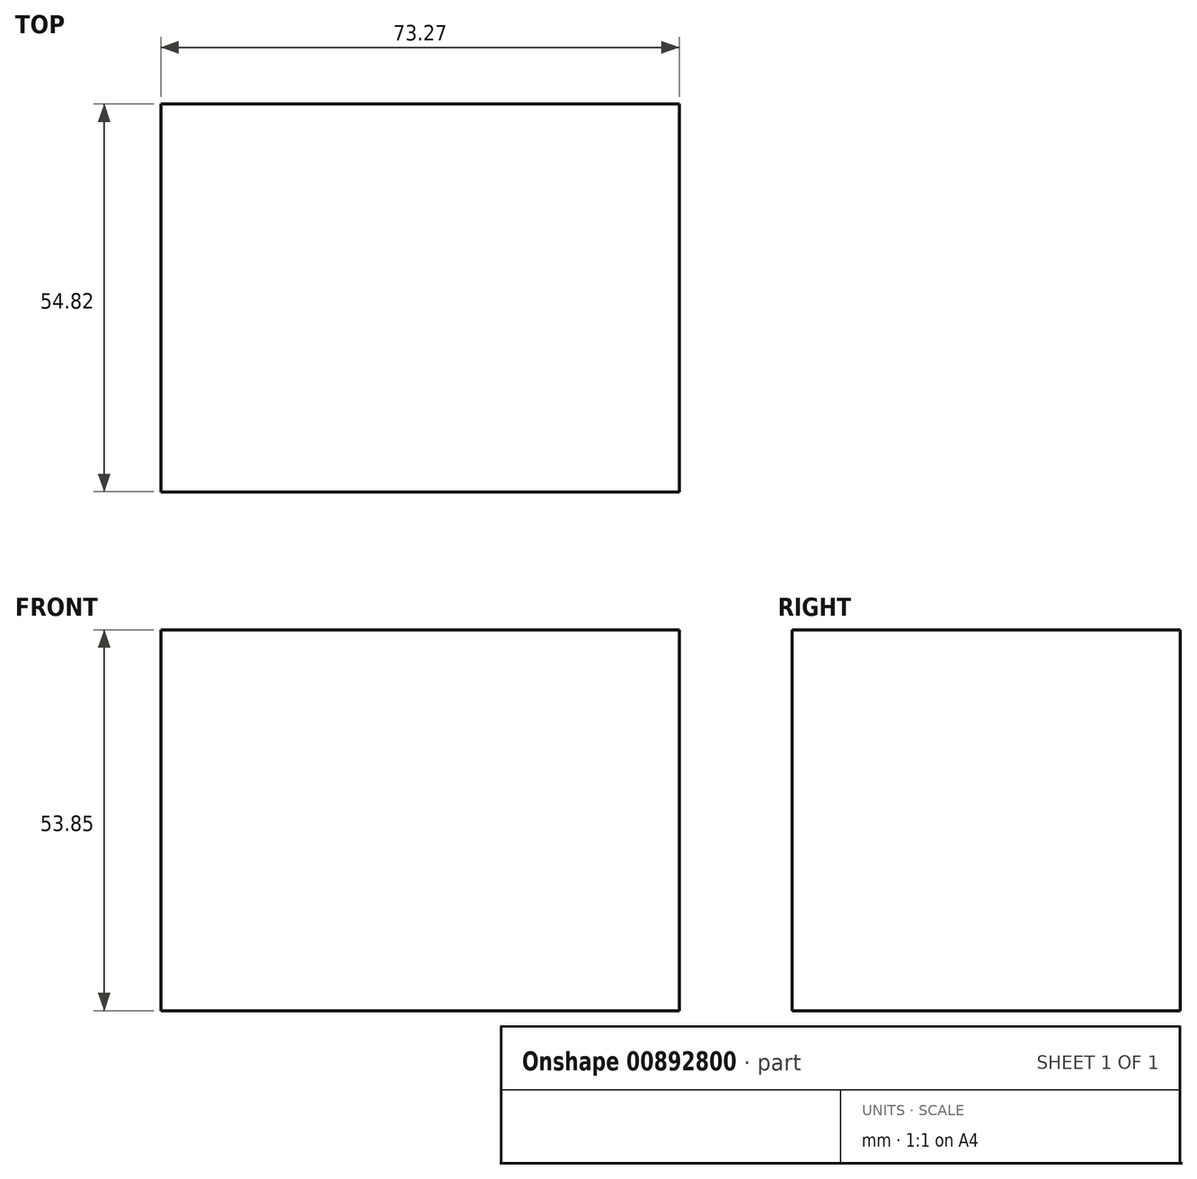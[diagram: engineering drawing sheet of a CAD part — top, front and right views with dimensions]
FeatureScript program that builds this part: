
annotation { "Feature Type Name" : "Feature", "Feature Type Description" : "" }
export const myFeature = defineFeature(function(context is Context, id is Id, definition is map)
    precondition{}
    {
        {
            var Q0;
            Q0=qCreatedBy(makeId("Top.planeOp"),FACE);
            var sketch = newSketch(context, id + "F0", { "sketchPlane" : qUnion([Q0])});
            skLineSegment(sketch, "E0.bottom", {"start": v(-46.26, 31.62) * mm, "end": v(27.01, 31.62) * mm});
            skLineSegment(sketch, "E0.top", {"start": v(-46.26, -23.2) * mm, "end": v(27.01, -23.2) * mm});
            skLineSegment(sketch, "E0.left", {"start": v(-46.26, 31.62) * mm, "end": v(-46.26, -23.2) * mm});
            skLineSegment(sketch, "E0.right", {"start": v(27.01, 31.62) * mm, "end": v(27.01, -23.2) * mm});
            skSolve(sketch);
        }
        {
            var Q0;
            Q0 = qSketchRegion(id + "F0", true);
            extrude(context, id + "F1", {"entities" : qUnion([Q0]), "depth" : 53.85 * mm, "offsetDistance" : 25.4 * mm});
        }
    });
